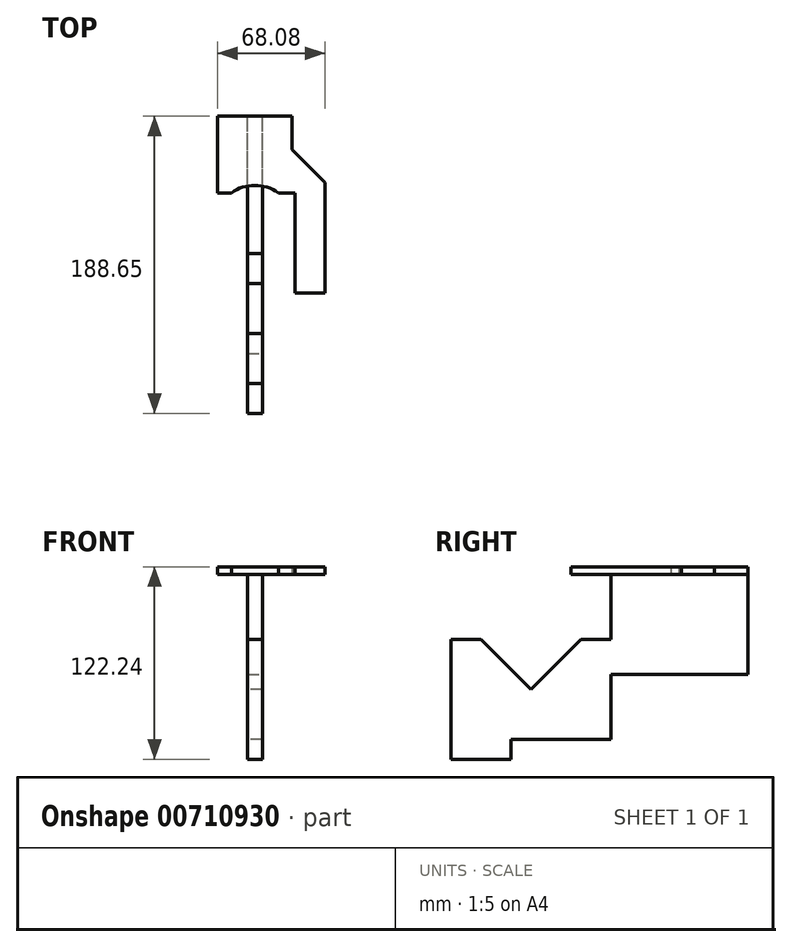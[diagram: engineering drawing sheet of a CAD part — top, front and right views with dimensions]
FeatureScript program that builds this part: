
annotation { "Feature Type Name" : "Feature", "Feature Type Description" : "" }
export const myFeature = defineFeature(function(context is Context, id is Id, definition is map)
    precondition{}
    {
        {
            var Q0;
            Q0=qCreatedBy(makeId("Right.planeOp"),FACE);
            var sketch = newSketch(context, id + "F0", { "sketchPlane" : qUnion([Q0])});
            skLineSegment(sketch, "E0.bottom", {"start": v(-25.4, 63.5) * mm, "end": v(-127, 63.5) * mm});
            skLineSegment(sketch, "E0.top", {"start": v(-25.4, 127) * mm, "end": v(-44.45, 127) * mm});
            skLineSegment(sketch, "E0.left", {"start": v(-25.4, 63.5) * mm, "end": v(-25.4, 127) * mm});
            skLineSegment(sketch, "E0.right", {"start": v(-127, 63.5) * mm, "end": v(-127, 127) * mm});
            skLineSegment(sketch, "E1", {"start": v(-107.95, 127) * mm, "end": v(-76.2, 95.25) * mm});
            skLineSegment(sketch, "E2", {"start": v(-76.2, 95.25) * mm, "end": v(-44.45, 127) * mm});
            skLineSegment(sketch, "E3.trimOffspring", {"start": v(-107.95, 127) * mm, "end": v(-127, 127) * mm});
            skSolve(sketch);
        }
        {
            var Q0;
            Q0=qSketchRegion(id+"F0",true);
            extrude(context, id + "F1", {"entities" : qUnion([Q0]), "depth" : 9.52 * mm, "offsetDistance" : 25.4 * mm});
        }
        {
            var Q0;
            Q0=makeQuery(id+"F1.opExtrude","SWEPT_BODY",BODY,{"disambiguationData":[OSD([sQuery(id+"F0.wireOp",EDGE,"E0.bottom"),sQuery(id+"F0.wireOp",EDGE,"E0.top"),sQuery(id+"F0.wireOp",EDGE,"E0.left"),sQuery(id+"F0.wireOp",EDGE,"E0.right"),sQuery(id+"F0.wireOp",EDGE,"E1"),sQuery(id+"F0.wireOp",EDGE,"E2"),sQuery(id+"F0.wireOp",EDGE,"E3.trimOffspring")])]});
            transform(context, id + "F2", {"entities" : qUnion([Q0]), "transformType" : TransformType.TRANSLATION_3D, "dx" : 25.4 * mm, "dy" : 88.9 * mm, "dz" : 0 * mm, "makeCopy" : false});
        }
        {
            var Q0;
            Q0=makeQuery(id+"F1.opExtrude","CAP_FACE",FACE,{"disambiguationData":[OSD([sQuery(id+"F0.wireOp",EDGE,"E0.bottom"),sQuery(id+"F0.wireOp",EDGE,"E0.top"),sQuery(id+"F0.wireOp",EDGE,"E0.left"),sQuery(id+"F0.wireOp",EDGE,"E0.right"),sQuery(id+"F0.wireOp",EDGE,"E1"),sQuery(id+"F0.wireOp",EDGE,"E2"),sQuery(id+"F0.wireOp",EDGE,"E3.trimOffspring")])],"isStart":false});
            var sketch = newSketch(context, id + "F3", { "sketchPlane" : qUnion([Q0])});
            skLineSegment(sketch, "E4.bottom", {"start": v(63.5, 168.28) * mm, "end": v(150.55, 168.28) * mm});
            skLineSegment(sketch, "E4.top", {"start": v(63.5, 104.78) * mm, "end": v(150.55, 104.78) * mm});
            skLineSegment(sketch, "E4.left", {"start": v(63.5, 168.28) * mm, "end": v(63.5, 104.78) * mm});
            skLineSegment(sketch, "E4.right", {"start": v(150.55, 168.28) * mm, "end": v(150.55, 104.78) * mm});
            skLineSegment(sketch, "E5.bottom", {"start": v(-38.1, 63.5) * mm, "end": v(0, 63.5) * mm});
            skLineSegment(sketch, "E5.top", {"start": v(-38.1, 50.8) * mm, "end": v(0, 50.8) * mm});
            skLineSegment(sketch, "E5.left", {"start": v(-38.1, 63.5) * mm, "end": v(-38.1, 50.8) * mm});
            skLineSegment(sketch, "E5.right", {"start": v(0, 63.5) * mm, "end": v(0, 50.8) * mm});
            skSolve(sketch);
        }
        {
            var Q0;
            Q0=qSketchRegion(id+"F3",true);
            extrude(context, id + "F4", {"entities" : qUnion([Q0]), "operationType" : NewBodyOperationType.ADD, "oppositeDirection" : true, "depth" : 9.52 * mm, "offsetDistance" : 25.4 * mm});
        }
        {
            var Q0;
            Q0=makeQuery(id+"F4.opExtrude","SWEPT_FACE",FACE,{"disambiguationData":[OSD([sQuery(id+"F3.wireOp",EDGE,"E4.bottom")])]});
            var sketch = newSketch(context, id + "F5", { "sketchPlane" : qUnion([Q0])});
            skLineSegment(sketch, "E6.bottom", {"start": v(6.54, 108.2) * mm, "end": v(53.78, 108.2) * mm});
            skLineSegment(sketch, "E6.top", {"start": v(6.54, 150.55) * mm, "end": v(53.78, 150.55) * mm});
            skLineSegment(sketch, "E6.left", {"start": v(6.54, 108.2) * mm, "end": v(6.54, 150.55) * mm});
            skLineSegment(sketch, "E6.right", {"start": v(53.78, 108.2) * mm, "end": v(53.78, 150.55) * mm});
            skLineSegment(sketch, "E7", {"start": v(53.78, 129.37) * mm, "end": v(74.61, 108.55) * mm});
            skLineSegment(sketch, "E8", {"start": v(74.61, 108.55) * mm, "end": v(74.61, 38.35) * mm});
            skLineSegment(sketch, "E9", {"start": v(74.61, 38.35) * mm, "end": v(55.56, 38.35) * mm});
            skLineSegment(sketch, "E10", {"start": v(55.56, 38.35) * mm, "end": v(55.56, 101.85) * mm});
            skLineSegment(sketch, "E11", {"start": v(55.56, 101.85) * mm, "end": v(45.06, 101.85) * mm});
            skLineSegment(sketch, "E12", {"start": v(6.53, 101.85) * mm, "end": v(6.54, 108.2) * mm});
            skArc(sketch, "E13", {"start": v(45.06, 101.85) * mm, "mid": v(30.16, 106.68) * mm, "end": v(15.27, 101.85) * mm});
            skLineSegment(sketch, "E14.trimOffspring", {"start": v(15.27, 101.85) * mm, "end": v(6.53, 101.85) * mm});
            skSolve(sketch);
        }
        {
            var Q0;
            Q0=qSketchRegion(id+"F5",true);
            extrude(context, id + "F6", {"entities" : qUnion([Q0]), "operationType" : NewBodyOperationType.ADD, "depth" : 4.76 * mm, "offsetDistance" : 25.4 * mm});
        }
    });
